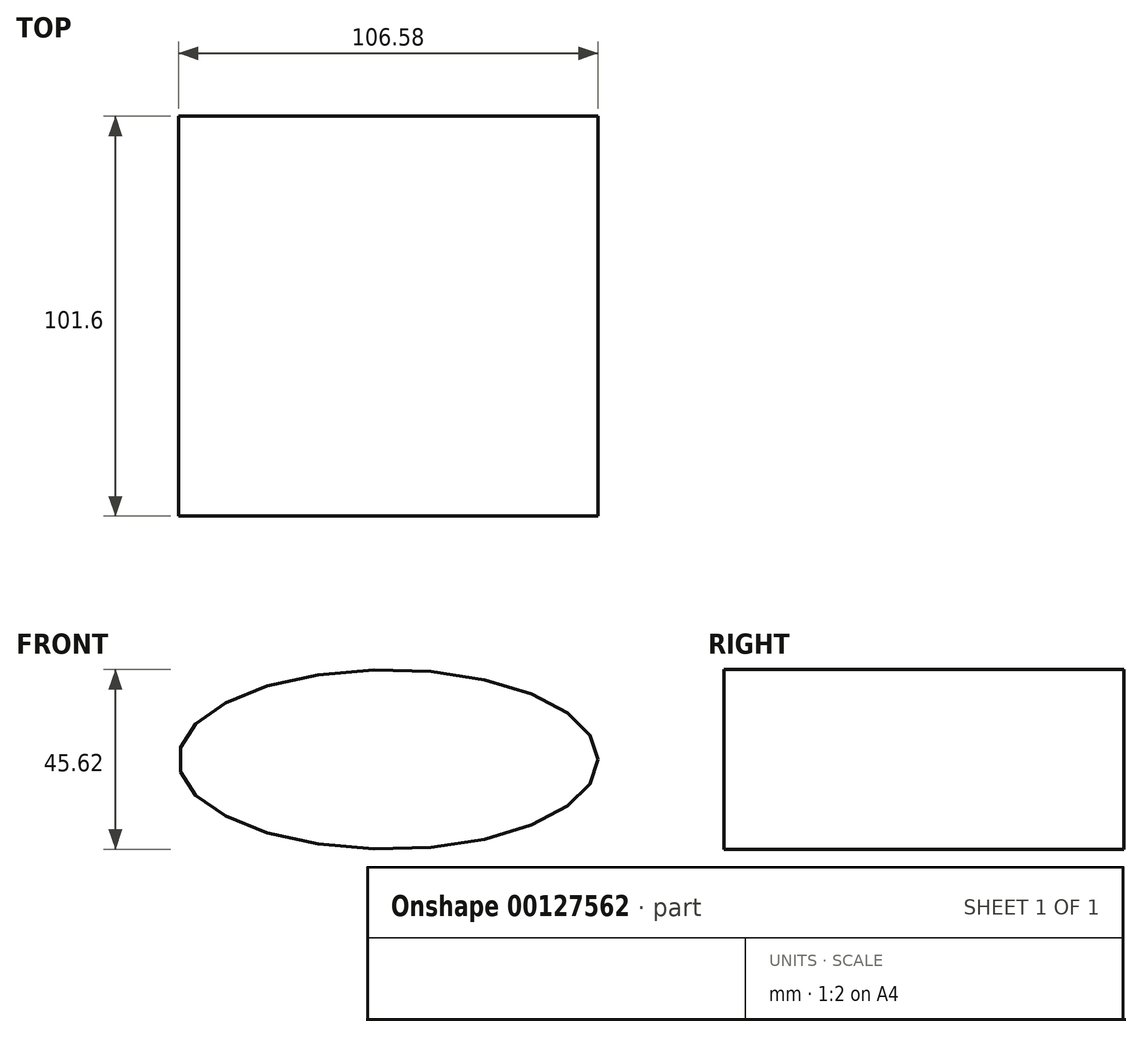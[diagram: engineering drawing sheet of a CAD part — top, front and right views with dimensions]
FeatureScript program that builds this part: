
annotation { "Feature Type Name" : "Feature", "Feature Type Description" : "" }
export const myFeature = defineFeature(function(context is Context, id is Id, definition is map)
    precondition{}
    {
        {
            var Q0;
            Q0=qCreatedBy(makeId("Front.planeOp"),FACE);
            var sketch = newSketch(context, id + "F0", { "sketchPlane" : qUnion([Q0])});
            skEllipse(sketch, "E0", {"center": v(0, 0) * mm, "majorRadius": 53.29 * mm, "minorRadius": 22.81 * mm, "majorAxis": v(1, 0)});
            skCircle(sketch, "E1", {"center": v(-22.7, 0) * mm, "radius": 11.7 * mm});
            skCircle(sketch, "E2", {"center": v(20.23, 0) * mm, "radius": 7.94 * mm});
            skSolve(sketch);
        }
        {
            var Q0;
            Q0=makeQuery(id+"F0.imprint","IMPRINT",FACE,{"disambiguationData":[TD([[makeQuery(id+"F0.imprint","IMPRINT",EDGE,{"derivedFrom":sQuery(id+"F0.wireOp",EDGE,"E2")}),1.0]])]});
            var Q1;
            Q1=makeQuery(id+"F0.imprint","IMPRINT",FACE,{"disambiguationData":[TD([[makeQuery(id+"F0.imprint","IMPRINT",EDGE,{"derivedFrom":sQuery(id+"F0.wireOp",EDGE,"E1")}),1.0]])]});
            var Q2;
            Q2=makeQuery(id+"F0.imprint","IMPRINT",FACE,{"disambiguationData":[TD([[makeQuery(id+"F0.imprint","IMPRINT",EDGE,{"derivedFrom":sQuery(id+"F0.wireOp",EDGE,"E0")}),1.0]])]});
            extrude(context, id + "F1", {"entities" : qUnion([Q0, Q1, Q2]), "depth" : 101.6 * mm});
        }
    });
